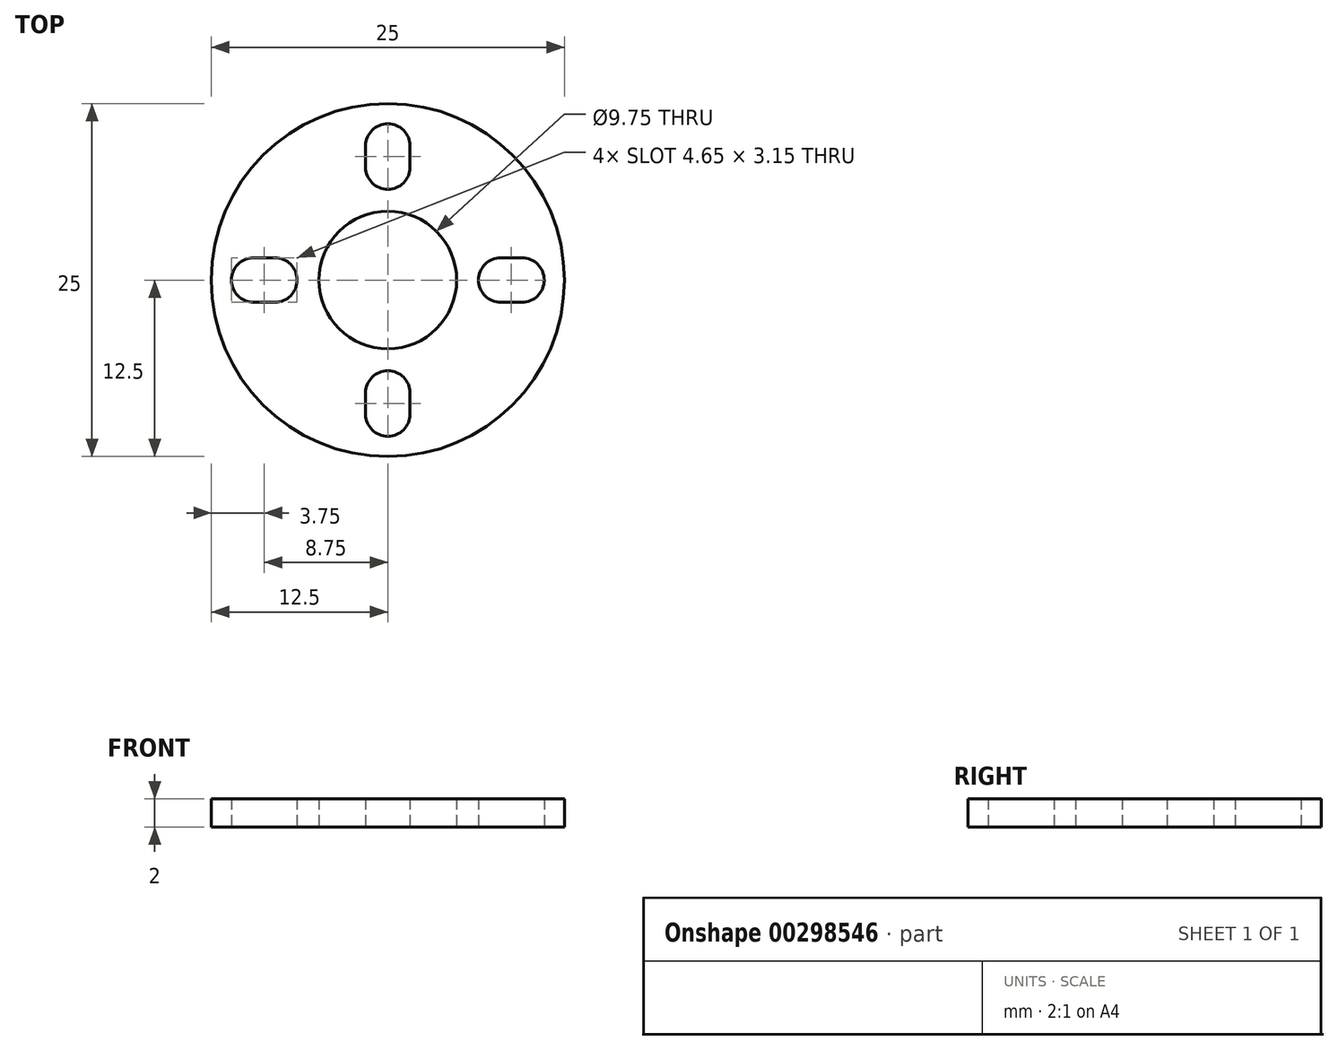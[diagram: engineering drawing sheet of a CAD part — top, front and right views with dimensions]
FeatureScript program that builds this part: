
annotation { "Feature Type Name" : "Feature", "Feature Type Description" : "" }
export const myFeature = defineFeature(function(context is Context, id is Id, definition is map)
    precondition{}
    {
        {
            var Q0;
            Q0=qCreatedBy(makeId("Top.planeOp"),FACE);
            var sketch = newSketch(context, id + "F0", { "sketchPlane" : qUnion([Q0])});
            skCircle(sketch, "E0", {"center": v(0, 0) * mm, "radius": 12.5 * mm});
            skCircle(sketch, "E1", {"center": v(0, 0) * mm, "radius": 9.5 * mm, "construction": true});
            skCircle(sketch, "E2", {"center": v(0, 0) * mm, "radius": 8 * mm, "construction": true});
            skCircle(sketch, "E3", {"center": v(0, 0) * mm, "radius": 4.88 * mm});
            skLineSegment(sketch, "E4", {"start": v(0, 8) * mm, "end": v(0, 9.5) * mm, "construction": true});
            skArc(sketch, "E5.0.startCap", {"start": v(1.57, 8) * mm, "mid": v(0, 6.42) * mm, "end": v(-1.57, 8) * mm});
            skArc(sketch, "E5.0.endCap", {"start": v(-1.57, 9.5) * mm, "mid": v(0, 11.07) * mm, "end": v(1.57, 9.5) * mm});
            skLineSegment(sketch, "E5.0.left", {"start": v(-1.57, 8) * mm, "end": v(-1.57, 9.5) * mm});
            skLineSegment(sketch, "E5.0.right", {"start": v(1.57, 8) * mm, "end": v(1.57, 9.5) * mm});
            skLineSegment(sketch, "E6", {"start": v(-43.45, 0) * mm, "end": v(36.12, 0) * mm, "construction": true});
            skLineSegment(sketch, "E7", {"start": v(-22.35, 22.35) * mm, "end": v(16.9, -16.9) * mm, "construction": true});
            skLineSegment(sketch, "E8.MirrorCS", {"start": v(1.57, -8) * mm, "end": v(1.57, -9.5) * mm});
            skArc(sketch, "E9.MirrorCS", {"start": v(-1.57, -9.5) * mm, "mid": v(0, -11.07) * mm, "end": v(1.57, -9.5) * mm});
            skLineSegment(sketch, "E10.MirrorCS", {"start": v(-1.57, -8) * mm, "end": v(-1.57, -9.5) * mm});
            skArc(sketch, "E11.MirrorCS", {"start": v(1.57, -8) * mm, "mid": v(0, -6.42) * mm, "end": v(-1.57, -8) * mm});
            skArc(sketch, "E12.MirrorCS", {"start": v(-9.5, 1.57) * mm, "mid": v(-11.07, 0) * mm, "end": v(-9.5, -1.58) * mm});
            skLineSegment(sketch, "E13.MirrorCS", {"start": v(-8, -1.58) * mm, "end": v(-9.5, -1.58) * mm});
            skLineSegment(sketch, "E14.MirrorCS", {"start": v(-8, 1.57) * mm, "end": v(-9.5, 1.57) * mm});
            skArc(sketch, "E15.MirrorCS", {"start": v(-8, -1.58) * mm, "mid": v(-6.42, 0) * mm, "end": v(-8, 1.57) * mm});
            skArc(sketch, "E16.MirrorCS", {"start": v(8, -1.57) * mm, "mid": v(6.42, 0) * mm, "end": v(8, 1.58) * mm});
            skLineSegment(sketch, "E17.MirrorCS", {"start": v(8, 1.58) * mm, "end": v(9.5, 1.58) * mm});
            skLineSegment(sketch, "E18.MirrorCS", {"start": v(8, -1.57) * mm, "end": v(9.5, -1.57) * mm});
            skArc(sketch, "E19.MirrorCS", {"start": v(9.5, 1.58) * mm, "mid": v(11.07, 0) * mm, "end": v(9.5, -1.57) * mm});
            skSolve(sketch);
        }
        {
            var Q0;
            Q0 = qSketchRegion(id + "F0", true);
            extrude(context, id + "F1", {"entities" : qUnion([Q0]), "offsetDistance" : 25 * mm, "depth" : 2 * mm});
        }
    });
